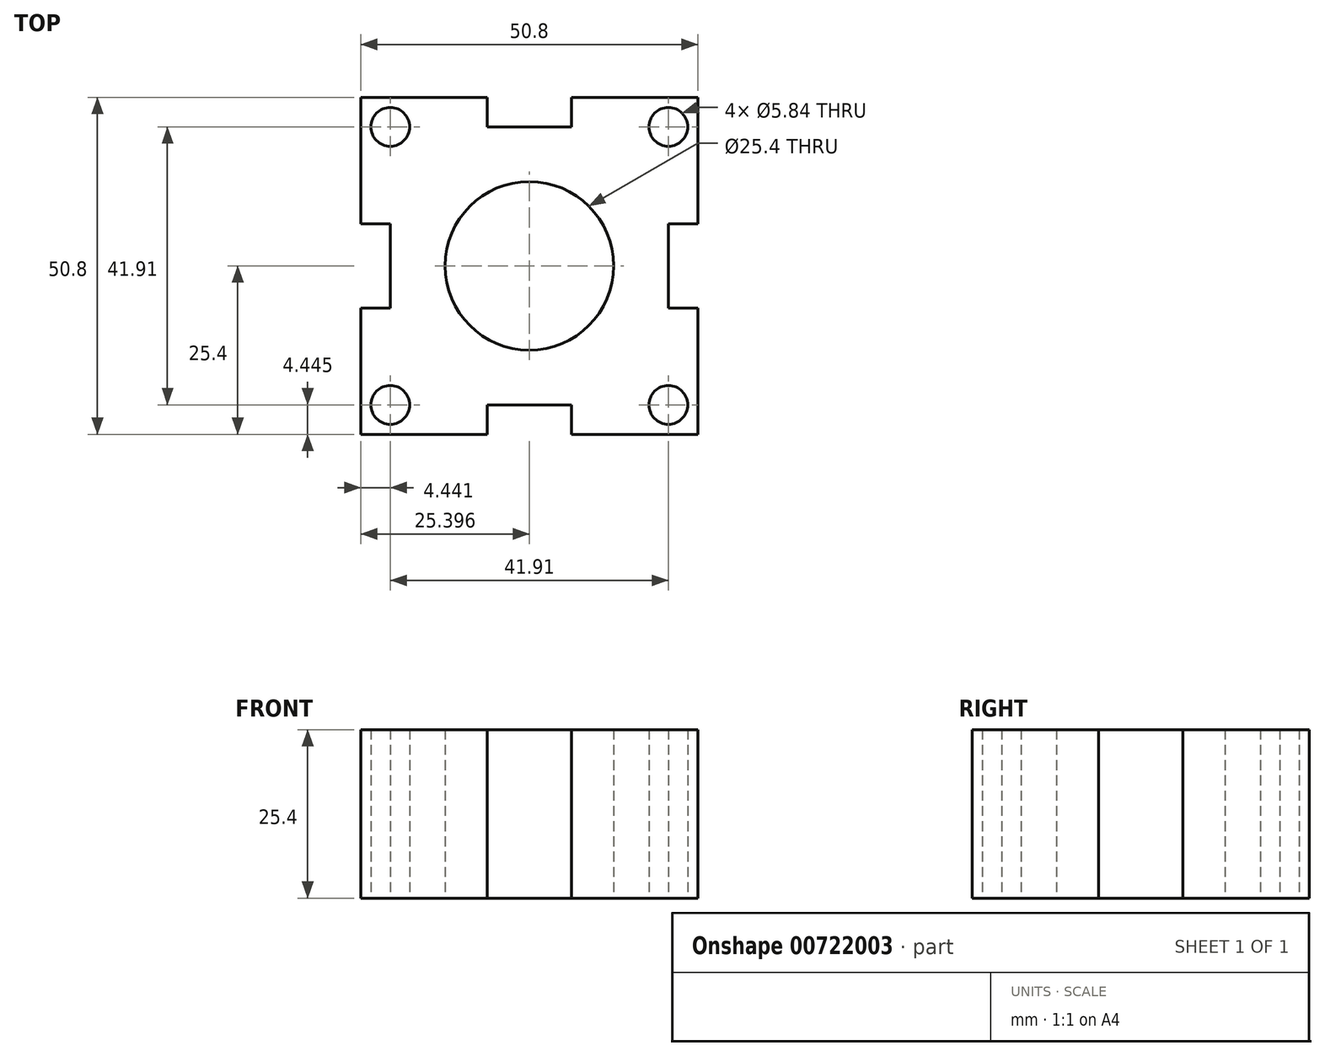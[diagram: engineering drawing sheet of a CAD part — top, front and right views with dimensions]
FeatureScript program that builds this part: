
annotation { "Feature Type Name" : "Feature", "Feature Type Description" : "" }
export const myFeature = defineFeature(function(context is Context, id is Id, definition is map)
    precondition{}
    {
        {
            var Q0;
            Q0=qCreatedBy(makeId("Top.planeOp"),FACE);
            var sketch = newSketch(context, id + "F0", { "sketchPlane" : qUnion([Q0])});
            skLineSegment(sketch, "E0.bottom", {"start": v(12.09, 25.4) * mm, "end": v(31.14, 25.4) * mm});
            skLineSegment(sketch, "E0.top", {"start": v(12.09, -25.4) * mm, "end": v(31.14, -25.4) * mm});
            skLineSegment(sketch, "E0.left", {"start": v(12.09, 25.4) * mm, "end": v(12.09, 6.35) * mm});
            skLineSegment(sketch, "E0.right", {"start": v(62.89, 25.4) * mm, "end": v(62.89, 6.35) * mm});
            skCircle(sketch, "E1", {"center": v(37.49, 0) * mm, "radius": 12.7 * mm});
            skLineSegment(sketch, "E2", {"start": v(31.14, -25.4) * mm, "end": v(31.14, -20.95) * mm});
            skLineSegment(sketch, "E3", {"start": v(31.14, -20.95) * mm, "end": v(43.84, -20.95) * mm});
            skLineSegment(sketch, "E4", {"start": v(43.84, -20.95) * mm, "end": v(43.84, -25.4) * mm});
            skLineSegment(sketch, "E5.trimOffspring", {"start": v(43.84, -25.4) * mm, "end": v(62.89, -25.4) * mm});
            skLineSegment(sketch, "E6", {"start": v(12.09, 6.35) * mm, "end": v(16.53, 6.35) * mm});
            skLineSegment(sketch, "E7", {"start": v(16.53, 6.35) * mm, "end": v(16.53, -6.35) * mm});
            skLineSegment(sketch, "E8", {"start": v(16.53, -6.35) * mm, "end": v(12.09, -6.35) * mm});
            skLineSegment(sketch, "E9.trimOffspring", {"start": v(12.09, -6.35) * mm, "end": v(12.09, -25.4) * mm});
            skLineSegment(sketch, "E10.top", {"start": v(31.14, 20.96) * mm, "end": v(43.84, 20.96) * mm});
            skLineSegment(sketch, "E10.left", {"start": v(31.14, 25.4) * mm, "end": v(31.14, 20.96) * mm});
            skLineSegment(sketch, "E10.right", {"start": v(43.84, 25.4) * mm, "end": v(43.84, 20.96) * mm});
            skLineSegment(sketch, "E11.trimOffspring", {"start": v(43.84, 25.4) * mm, "end": v(62.89, 25.4) * mm});
            skLineSegment(sketch, "E12.bottom", {"start": v(62.89, 6.35) * mm, "end": v(58.44, 6.35) * mm});
            skLineSegment(sketch, "E12.top", {"start": v(62.89, -6.35) * mm, "end": v(58.44, -6.35) * mm});
            skLineSegment(sketch, "E12.right", {"start": v(58.44, 6.35) * mm, "end": v(58.44, -6.35) * mm});
            skLineSegment(sketch, "E13.trimOffspring", {"start": v(62.89, -6.35) * mm, "end": v(62.89, -25.4) * mm});
            skCircle(sketch, "E14", {"center": v(58.44, 20.96) * mm, "radius": 2.92 * mm});
            skCircle(sketch, "E15", {"center": v(16.53, 20.96) * mm, "radius": 2.92 * mm});
            skCircle(sketch, "E16", {"center": v(58.44, -20.95) * mm, "radius": 2.92 * mm});
            skCircle(sketch, "E17", {"center": v(16.53, -20.95) * mm, "radius": 2.92 * mm});
            skSolve(sketch);
        }
        {
            var Q0;
            Q0 = qSketchRegion(id + "F0", true);
            extrude(context, id + "F1", {"entities" : qUnion([Q0]), "depth" : 25.4 * mm, "offsetDistance" : 25.4 * mm});
        }
        {
            var Q0;
            Q0=sQuery(id+"F0.wireOp",EDGE,"E11.trimOffspring");
            var Q1;
            Q1=sQuery(id+"F0.wireOp",EDGE,"E17");
            var Q2;
            Q2=sQuery(id+"F0.wireOp",EDGE,"E0.bottom");
            var Q3;
            Q3=sQuery(id+"F0.wireOp",EDGE,"E0.left");
            var Q4;
            Q4=sQuery(id+"F0.wireOp",EDGE,"E0.right");
            var Q5;
            Q5=sQuery(id+"F0.wireOp",EDGE,"E1");
            var Q6;
            Q6=sQuery(id+"F0.wireOp",EDGE,"E3");
            var Q7;
            Q7=sQuery(id+"F0.wireOp",EDGE,"E5.trimOffspring");
            var Q8;
            Q8=sQuery(id+"F0.wireOp",EDGE,"E7");
            var Q9;
            Q9=sQuery(id+"F0.wireOp",EDGE,"E16");
            var Q10;
            Q10=sQuery(id+"F0.wireOp",EDGE,"E9.trimOffspring");
            var Q11;
            Q11=sQuery(id+"F0.wireOp",EDGE,"E14");
            var Q12;
            Q12=sQuery(id+"F0.wireOp",EDGE,"E12.right");
            var Q13;
            Q13=sQuery(id+"F0.wireOp",EDGE,"E10.top");
            var Q14;
            Q14=sQuery(id+"F0.wireOp",EDGE,"E0.top");
            var Q15;
            Q15=sQuery(id+"F0.wireOp",EDGE,"E13.trimOffspring");
            var Q16;
            Q16=sQuery(id+"F0.wireOp",EDGE,"E15");
            var Q17;
            Q17=sQuery(id+"F0.wireOp",EDGE,"E10.right");
            var Q18;
            Q18=sQuery(id+"F0.wireOp",EDGE,"E4");
            var Q19;
            Q19=sQuery(id+"F0.wireOp",EDGE,"E6");
            var Q20;
            Q20=sQuery(id+"F0.wireOp",EDGE,"E8");
            var Q21;
            Q21=sQuery(id+"F0.wireOp",EDGE,"E12.top");
            var Q22;
            Q22=sQuery(id+"F0.wireOp",EDGE,"E12.bottom");
            var Q23;
            Q23=sQuery(id+"F0.wireOp",EDGE,"E10.left");
            var Q24;
            Q24=sQuery(id+"F0.wireOp",EDGE,"E2");
            extrude(context, id + "F2", {"bodyType" : ToolBodyType.SURFACE, "surfaceEntities" : qUnion([Q0, Q1, Q2, Q3, Q4, Q5, Q6, Q7, Q8, Q9, Q10, Q11, Q12, Q13, Q14, Q15, Q16, Q17, Q18, Q19, Q20, Q21, Q22, Q23, Q24]), "depth" : 25.4 * mm, "offsetDistance" : 25.4 * mm});
        }
    });
